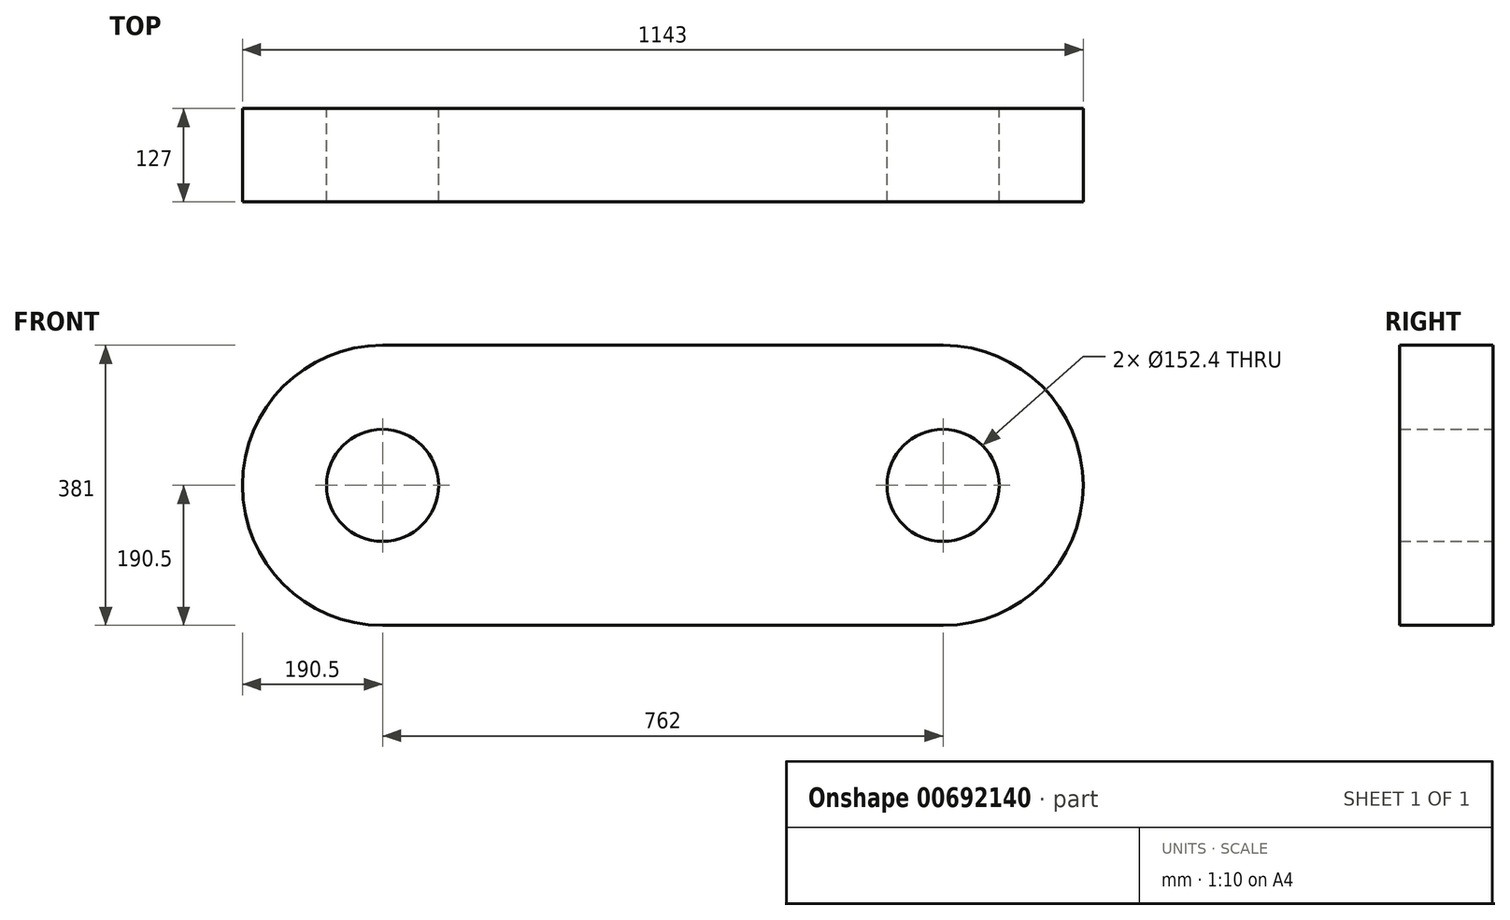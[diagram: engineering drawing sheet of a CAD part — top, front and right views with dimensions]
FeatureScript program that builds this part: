
annotation { "Feature Type Name" : "Feature", "Feature Type Description" : "" }
export const myFeature = defineFeature(function(context is Context, id is Id, definition is map)
    precondition{}
    {
        {
            var Q0;
            Q0=qCreatedBy(makeId("Front.planeOp"),FACE);
            var sketch = newSketch(context, id + "F0", { "sketchPlane" : qUnion([Q0])});
            skLineSegment(sketch, "E0.bottom", {"start": v(-381, 190.5) * mm, "end": v(381, 190.5) * mm});
            skLineSegment(sketch, "E0.top", {"start": v(-381, -190.5) * mm, "end": v(381, -190.5) * mm});
            skLineSegment(sketch, "E0.left", {"start": v(-381, 190.5) * mm, "end": v(-381, -190.5) * mm, "construction": true});
            skLineSegment(sketch, "E0.right", {"start": v(381, 190.5) * mm, "end": v(381, -190.5) * mm, "construction": true});
            skArc(sketch, "E1", {"start": v(-381, 190.5) * mm, "mid": v(-571.5, 0) * mm, "end": v(-381, -190.5) * mm});
            skArc(sketch, "E2.MirrorCS", {"start": v(381, 190.5) * mm, "mid": v(571.5, 0) * mm, "end": v(381, -190.5) * mm});
            skCircle(sketch, "E3", {"center": v(-381, 0) * mm, "radius": 76.2 * mm});
            skCircle(sketch, "E4", {"center": v(381, 0) * mm, "radius": 76.2 * mm});
            skSolve(sketch);
        }
        {
            var Q0;
            Q0=qSketchRegion(id+"F0",true);
            extrude(context, id + "F1", {"entities" : qUnion([Q0]), "depth" : 127 * mm, "offsetDistance" : 25.4 * mm});
        }
    });
